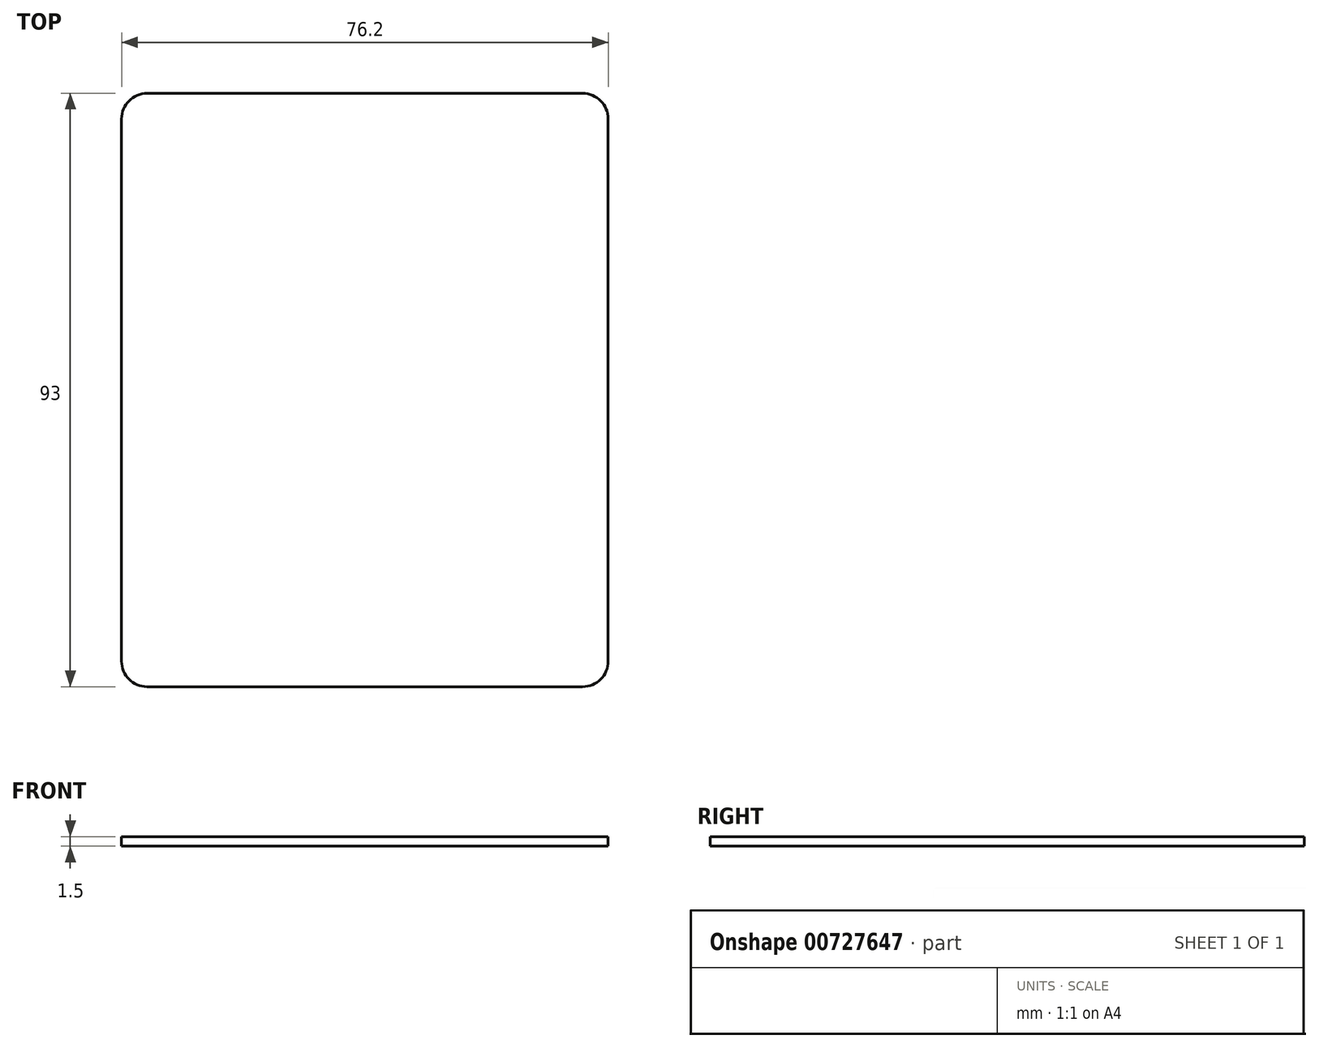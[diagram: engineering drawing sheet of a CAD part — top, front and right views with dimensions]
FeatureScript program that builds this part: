
annotation { "Feature Type Name" : "Feature", "Feature Type Description" : "" }
export const myFeature = defineFeature(function(context is Context, id is Id, definition is map)
    precondition{}
    {
        {
            var Q0;
            Q0=qCreatedBy(makeId("Top.planeOp"),FACE);
            var sketch = newSketch(context, id + "F0", { "sketchPlane" : qUnion([Q0])});
            skLineSegment(sketch, "E0", {"start": v(-32.71, 37.82) * mm, "end": v(35.49, 37.82) * mm});
            skLineSegment(sketch, "E1", {"start": v(-36.71, 33.82) * mm, "end": v(-36.71, -51.18) * mm});
            skLineSegment(sketch, "E2", {"start": v(-32.71, -55.18) * mm, "end": v(35.49, -55.18) * mm});
            skLineSegment(sketch, "E3", {"start": v(39.49, -51.18) * mm, "end": v(39.49, 33.82) * mm});
            skArc(sketch, "E4", {"start": v(39.49, 33.82) * mm, "mid": v(38.31, 36.65) * mm, "end": v(35.49, 37.82) * mm});
            skArc(sketch, "E5", {"start": v(-32.71, 37.82) * mm, "mid": v(-35.54, 36.65) * mm, "end": v(-36.71, 33.82) * mm});
            skArc(sketch, "E6", {"start": v(-36.71, -51.18) * mm, "mid": v(-35.54, -54.01) * mm, "end": v(-32.71, -55.18) * mm});
            skArc(sketch, "E7", {"start": v(39.49, -51.18) * mm, "mid": v(38.31, -54.01) * mm, "end": v(35.49, -55.18) * mm});
            skLineSegment(sketch, "E8", {"start": v(36.99, 35.32) * mm, "end": v(36.99, -52.68) * mm});
            skLineSegment(sketch, "E9", {"start": v(-34.21, -52.68) * mm, "end": v(36.99, -52.68) * mm});
            skLineSegment(sketch, "E10", {"start": v(-34.21, 35.32) * mm, "end": v(-34.21, -52.68) * mm});
            skLineSegment(sketch, "E11", {"start": v(-34.21, 35.32) * mm, "end": v(36.99, 35.32) * mm});
            skSolve(sketch);
        }
        {
            var Q0;
            Q0=makeQuery(id+"F0.imprint","IMPRINT",FACE,{"disambiguationData":[TD([[makeQuery(id+"F0.imprint","IMPRINT",EDGE,{"derivedFrom":sQuery(id+"F0.wireOp",EDGE,"E0")}),-1.0]])]});
            var Q1;
            Q1=makeQuery(id+"F0.imprint","IMPRINT",FACE,{"disambiguationData":[TD([[makeQuery(id+"F0.imprint","IMPRINT",EDGE,{"derivedFrom":sQuery(id+"F0.wireOp",EDGE,"E8")}),-1.0]])]});
            extrude(context, id + "F1", {"entities" : qUnion([Q0, Q1]), "depth" : 1.5 * mm, "offsetDistance" : 25 * mm});
        }
    });
